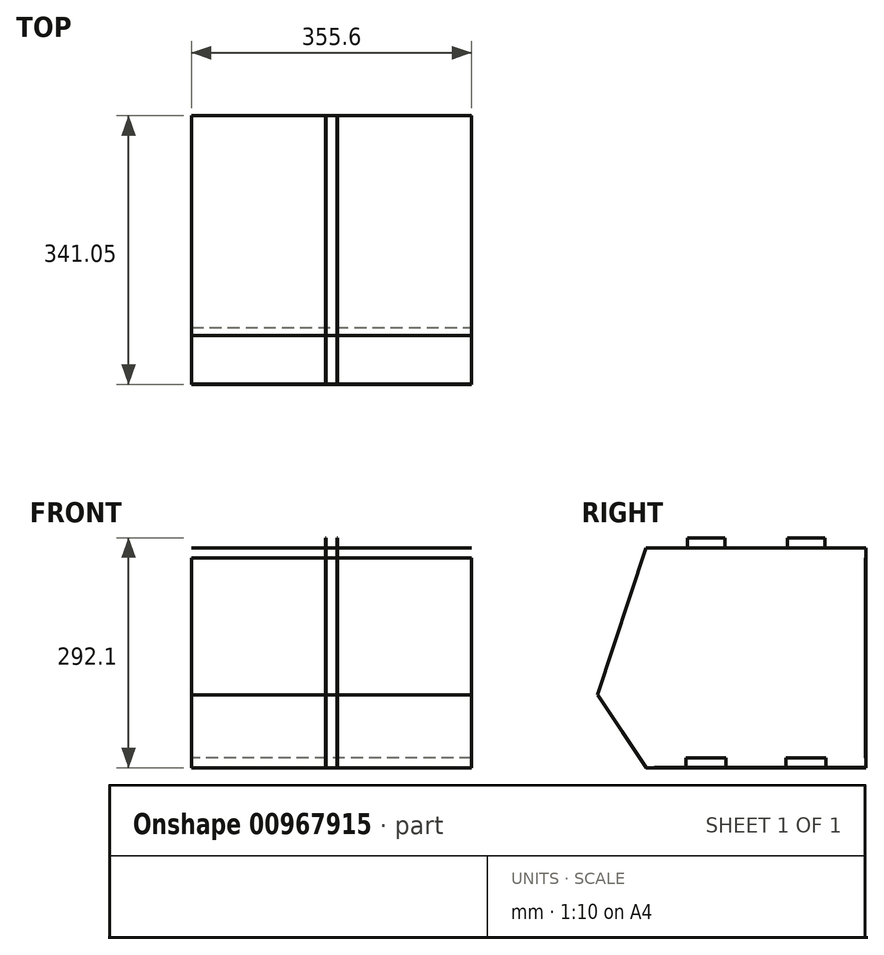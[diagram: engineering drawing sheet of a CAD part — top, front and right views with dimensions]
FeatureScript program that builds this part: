
annotation { "Feature Type Name" : "Feature", "Feature Type Description" : "" }
export const myFeature = defineFeature(function(context is Context, id is Id, definition is map)
    precondition{}
    {
        {
            assignVariable(context, id + "F0", {"name" : "thickness", "anyValue" : .5});
        }
        {
            assignVariable(context, id + "F1", {"name" : "width", "anyValue" : 14});
        }
        {
            var Q0;
            Q0=qCreatedBy(makeId("Right.planeOp"),FACE);
            var sketch = newSketch(context, id + "F2", { "sketchPlane" : qUnion([Q0])});
            skLineSegment(sketch, "E0", {"start": v(139.7, 139.7) * mm, "end": v(139.7, -139.7) * mm});
            skLineSegment(sketch, "E1", {"start": v(-139.7, -139.7) * mm, "end": v(-201.35, -47.25) * mm});
            skLineSegment(sketch, "E2", {"start": v(-201.35, -47.25) * mm, "end": v(-139.7, 139.7) * mm});
            skLineSegment(sketch, "E3", {"start": v(-139.7, -139.7) * mm, "end": v(-154.96, -139.7) * mm, "construction": true});
            skLineSegment(sketch, "E4", {"start": v(-154.96, -139.7) * mm, "end": v(-211.92, -54.3) * mm, "construction": true});
            skLineSegment(sketch, "E5", {"start": v(-211.92, -54.3) * mm, "end": v(-201.35, -47.25) * mm, "construction": true});
            skLineSegment(sketch, "E6", {"start": v(87.31, 139.7) * mm, "end": v(87.31, 152.4) * mm});
            skLineSegment(sketch, "E7", {"start": v(87.31, 152.4) * mm, "end": v(39.69, 152.4) * mm});
            skLineSegment(sketch, "E8", {"start": v(39.69, 152.4) * mm, "end": v(39.69, 139.7) * mm});
            skLineSegment(sketch, "E9", {"start": v(139.7, 139.7) * mm, "end": v(87.31, 139.7) * mm});
            skLineSegment(sketch, "E10", {"start": v(39.69, 139.7) * mm, "end": v(0, 139.7) * mm});
            skLineSegment(sketch, "E11", {"start": v(0, -139.7) * mm, "end": v(38.1, -139.7) * mm});
            skLineSegment(sketch, "E12", {"start": v(88.9, -127) * mm, "end": v(38.1, -127) * mm});
            skLineSegment(sketch, "E13", {"start": v(38.1, -127) * mm, "end": v(38.1, -139.7) * mm});
            skLineSegment(sketch, "E14", {"start": v(88.9, -127) * mm, "end": v(88.9, -139.7) * mm});
            skLineSegment(sketch, "E15", {"start": v(88.9, -139.7) * mm, "end": v(139.7, -139.7) * mm});
            skLineSegment(sketch, "E16.MirrorCS", {"start": v(-88.9, -139.7) * mm, "end": v(-139.7, -139.7) * mm});
            skLineSegment(sketch, "E17.MirrorCS", {"start": v(-88.9, -127) * mm, "end": v(-88.9, -139.7) * mm});
            skLineSegment(sketch, "E18.MirrorCS", {"start": v(-88.9, -127) * mm, "end": v(-38.1, -127) * mm});
            skLineSegment(sketch, "E19.MirrorCS", {"start": v(-38.1, -127) * mm, "end": v(-38.1, -139.7) * mm});
            skLineSegment(sketch, "E20.MirrorCS", {"start": v(0, -139.7) * mm, "end": v(-38.1, -139.7) * mm});
            skLineSegment(sketch, "E21.MirrorCS", {"start": v(-39.69, 152.4) * mm, "end": v(-39.69, 139.7) * mm});
            skLineSegment(sketch, "E22.MirrorCS", {"start": v(-87.31, 139.7) * mm, "end": v(-87.31, 152.4) * mm});
            skLineSegment(sketch, "E23.MirrorCS", {"start": v(-139.7, 139.7) * mm, "end": v(-87.31, 139.7) * mm});
            skLineSegment(sketch, "E24.MirrorCS", {"start": v(-87.31, 152.4) * mm, "end": v(-39.69, 152.4) * mm});
            skLineSegment(sketch, "E25.MirrorCS", {"start": v(-39.69, 139.7) * mm, "end": v(0, 139.7) * mm});
            skSolve(sketch);
        }
        {
            var Q0;
            Q0=qSketchRegion(id+"F2",true);
            extrude(context, id + "F3", {"entities" : qUnion([Q0]), "depth" : (getVariable(context, 'width') / 2 + getVariable(context, 'thickness')) * mm, "hasSecondDirection" : true, "secondDirectionOppositeDirection" : false, "secondDirectionDepth" : (getVariable(context, 'width') / 2) * mm});
        }
        {
            var Q0;
            Q0=makeQuery(id+"F3.opExtrude","SWEPT_BODY",BODY,{"disambiguationData":[OSD([sQuery(id+"F2.wireOp",EDGE,"E0"),sQuery(id+"F2.wireOp",EDGE,"uS7o3Ql0-Hwbm-FKSR-uhZp-ccV8yQ46O6f3"),sQuery(id+"F2.wireOp",EDGE,"E1"),sQuery(id+"F2.wireOp",EDGE,"E2"),sQuery(id+"F2.wireOp",EDGE,"c3iYRHqb-eUdC-9xOQ-NnuV-AFuO0mQXi6aF")])]});
            var Q1;
            Q1=qCreatedBy(makeId("Right.planeOp"),FACE);
            mirror(context, id + "F4", {"entities" : qUnion([Q0]), "mirrorPlane" : qUnion([Q1])});
        }
        {
            var Q0;
            Q0=makeQuery(id+"F3.opExtrude","SWEPT_FACE",FACE,{"disambiguationData":[OSD([sQuery(id+"F2.wireOp",EDGE,"E9")])]});
            var sketch = newSketch(context, id + "F5", { "sketchPlane" : qUnion([Q0])});
            skPoint(sketch, "E26.0", {"position": v(-177.8, 139.7) * mm});
            skPoint(sketch, "E27.0", {"position": v(177.8, -139.7) * mm});
            skLineSegment(sketch, "E28.bottom", {"start": v(-177.8, 139.7) * mm, "end": v(177.8, 139.7) * mm});
            skLineSegment(sketch, "E28.top", {"start": v(-177.8, -139.7) * mm, "end": v(177.8, -139.7) * mm});
            skLineSegment(sketch, "E28.left", {"start": v(-177.8, 139.7) * mm, "end": v(-177.8, -139.7) * mm});
            skLineSegment(sketch, "E28.right", {"start": v(177.8, 139.7) * mm, "end": v(177.8, -139.7) * mm});
            skSolve(sketch);
        }
        {
            var Q0;
            Q0=qSketchRegion(id+"F5",true);
            extrude(context, id + "F6", {"entities" : qUnion([Q0]), "oppositeDirection" : true, "depth" : (getVariable(context, 'thickness')) * mm});
        }
        {
            var Q0;
            Q0=makeQuery(id+"F4.opPattern","COPY",FACE,{"derivedFrom":makeQuery(id+"F3.opExtrude","SWEPT_FACE",FACE,{"disambiguationData":[OSD([sQuery(id+"F2.wireOp",EDGE,"E1")])]}),"instanceName":"1"});
            var sketch = newSketch(context, id + "F7", { "sketchPlane" : qUnion([Q0])});
            skPoint(sketch, "E29.0", {"position": v(-177.8, 72.4) * mm});
            skPoint(sketch, "E30.0", {"position": v(177.8, -38.72) * mm});
            skLineSegment(sketch, "E31.bottom", {"start": v(-177.8, 72.4) * mm, "end": v(177.8, 72.4) * mm});
            skLineSegment(sketch, "E31.top", {"start": v(-177.8, -38.72) * mm, "end": v(177.8, -38.72) * mm});
            skLineSegment(sketch, "E31.left", {"start": v(-177.8, 72.4) * mm, "end": v(-177.8, -38.72) * mm});
            skLineSegment(sketch, "E31.right", {"start": v(177.8, 72.4) * mm, "end": v(177.8, -38.72) * mm});
            skSolve(sketch);
        }
        {
            var Q0;
            Q0=makeQuery(id+"F7.imprint","IMPRINT",FACE,{"disambiguationData":[TD([[makeQuery(id+"F7.imprint","IMPRINT",EDGE,{"derivedFrom":sQuery(id+"F7.wireOp",EDGE,"E31.bottom")}),-1.0]])]});
            extrude(context, id + "F8", {"entities" : qUnion([Q0]), "oppositeDirection" : true, "depth" : (getVariable(context, 'thickness')) * mm});
        }
        {
            var Q0;
            Q0=makeQuery(id+"F3.opExtrude","SWEPT_FACE",FACE,{"disambiguationData":[OSD([sQuery(id+"F2.wireOp",EDGE,"E15")])]});
            var sketch = newSketch(context, id + "F9", { "sketchPlane" : qUnion([Q0])});
            skPoint(sketch, "E32.0", {"position": v(177.8, -139.7) * mm});
            skPoint(sketch, "E33.0", {"position": v(-177.8, 129.13) * mm});
            skLineSegment(sketch, "E34.bottom", {"start": v(-177.8, 129.13) * mm, "end": v(177.8, 129.13) * mm});
            skLineSegment(sketch, "E34.top", {"start": v(-177.8, -139.7) * mm, "end": v(177.8, -139.7) * mm});
            skLineSegment(sketch, "E34.left", {"start": v(-177.8, 129.13) * mm, "end": v(-177.8, -139.7) * mm});
            skLineSegment(sketch, "E34.right", {"start": v(177.8, 129.13) * mm, "end": v(177.8, -139.7) * mm});
            skSolve(sketch);
        }
        {
            var Q0;
            Q0=qSketchRegion(id+"F9",true);
            extrude(context, id + "F10", {"entities" : qUnion([Q0]), "oppositeDirection" : true, "depth" : (getVariable(context, 'thickness')) * mm});
        }
        {
            var Q0;
            Q0=makeQuery(id+"F3.opExtrude","SWEPT_FACE",FACE,{"disambiguationData":[OSD([sQuery(id+"F2.wireOp",EDGE,"E0")])]});
            var sketch = newSketch(context, id + "F11", { "sketchPlane" : qUnion([Q0])});
            skPoint(sketch, "E35.0", {"position": v(-177.8, 127) * mm});
            skPoint(sketch, "E36.0", {"position": v(177.8, -127) * mm});
            skLineSegment(sketch, "E37.bottom", {"start": v(-177.8, 127) * mm, "end": v(177.8, 127) * mm});
            skLineSegment(sketch, "E37.top", {"start": v(-177.8, -127) * mm, "end": v(177.8, -127) * mm});
            skLineSegment(sketch, "E37.left", {"start": v(-177.8, 127) * mm, "end": v(-177.8, -127) * mm});
            skLineSegment(sketch, "E37.right", {"start": v(177.8, 127) * mm, "end": v(177.8, -127) * mm});
            skSolve(sketch);
        }
        {
            var Q0;
            Q0=qSketchRegion(id+"F11",true);
            extrude(context, id + "F12", {"entities" : qUnion([Q0]), "oppositeDirection" : true, "depth" : (getVariable(context, 'thickness')) * mm});
        }
    });
